# Revit family: Toilet-Elongated_Transitional_UltraMax-II_MS604114CEF_TOTO
name_source: partatom
category: Plumbing Fixtures
revit_build: Autodesk Revit Architecture 2013 (Build: 20130531_2115(x64)
units: mm (PartAtom-declared; Revit-internal decimal feet)

## types (1)
- MS604114CEF
    04 CSI = 22 42 13
    95 CSI = 15410-800
    ADA Compliant = Yes
    Assembly Code = D2010110
    Bowl Material = Vitreous China
    CAD Drawing URL = http://assets.totousa.com
    CW Connection = Yes
    CWFU = 0
    Certifications = IAPMO (cUPC), State of Massachusetts, City of Los Angeles, and others
    Code Compliance = UPC, IPC, NSPC, NPC Canada, and others
    Cold Water Connection NPT Radius = 1/2"
    Color Availability = #01 Cotton, #03 Bone, #11 Colonial White, #12 Sedona Beige, #51 Ebony
    Default Elevation = 0"
    Description = UltraMax II Toilet, 1.28 GPF - ADA
    Finish = Vitreous China - TOTO - 01 Cotton
    Flush System = Double Cyclone
    Gallons Per Flush = 1.28 gal
    HW Connection = No
    HWFU = 0
    Height = 28 3/4"
    Industry Standards = Meets and exceeds ASME A112.19.2/CSA B45.1
    Length = 28 5/16"
    Manufacturer = TOTO USA, Inc.
    Manufacturer Fax = (770) 282-0002
    Model = MS604114CEF
    Mount Type = Floor-Mounted
    Rough in Availability = 12"
    Rough in Distance = 12"
    SanoGloss Available = No
    SanoGloss Note = Ebony not available in SanoGloss
    Series = UltraMax II
    Shipping Weight = 99.00 lb
    Spec Sheet URL = http://assets.totousa.com
    Style = Transitional
    Subcategory = Toilets
    Toto BIM Number = BM-00303
    URL = http://www.totousa.com
    Vent Connection = Yes
    WFU = 0
    Warranty = One Year Limited Warranty
    Warranty URL = http://www.totousa.com
    Waste Connection = Yes
    Waste Connection NPT Radius = 1 1/16"
    WaterSense = Yes
    Width = 16 9/16"
    ecoScorecard Product Page = http://toto.ecoscorecard.com
    ecoScorecard_data = http://toto.ecoscorecard.com

## geometry (parser evidence)
native form markers: Blend x6, Sweep x2
no freeform markers — native parametric forms only
